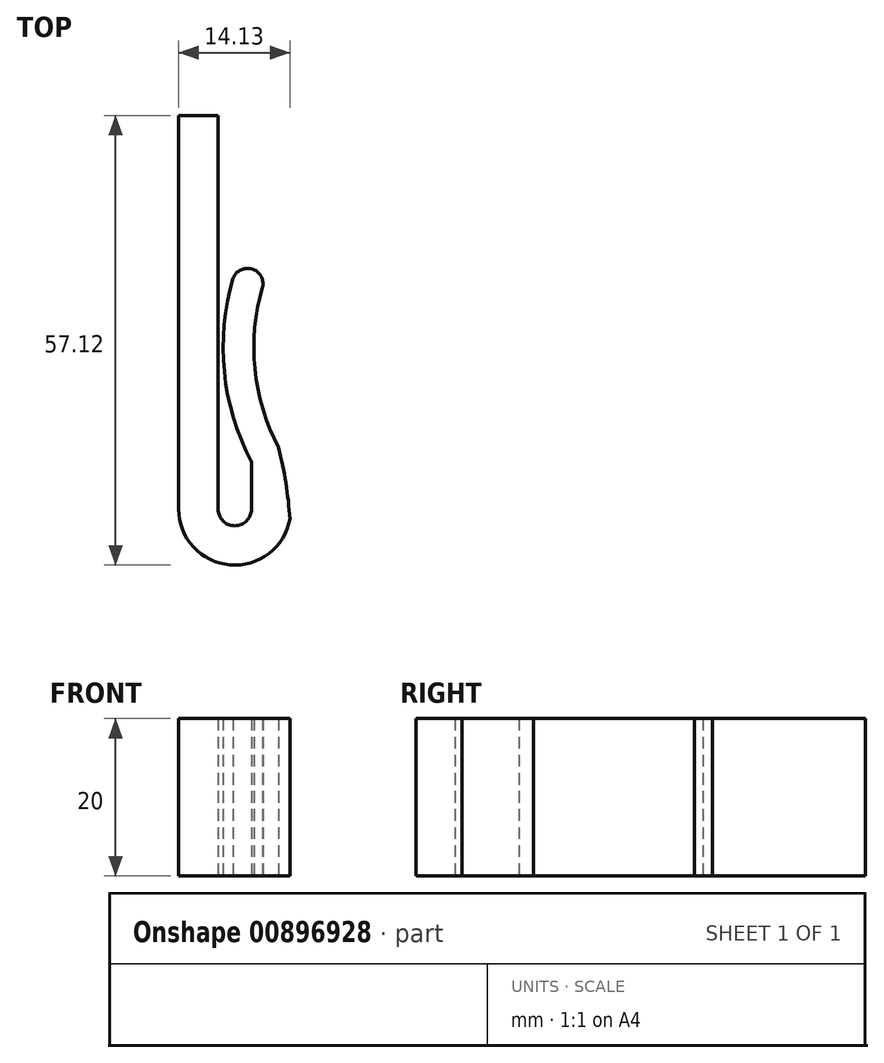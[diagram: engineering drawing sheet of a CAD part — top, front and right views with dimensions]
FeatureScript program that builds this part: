
annotation { "Feature Type Name" : "Feature", "Feature Type Description" : "" }
export const myFeature = defineFeature(function(context is Context, id is Id, definition is map)
    precondition{}
    {
        {
            var Q0;
            Q0=qCreatedBy(makeId("Top.planeOp"),FACE);
            var sketch = newSketch(context, id + "F0", { "sketchPlane" : qUnion([Q0])});
            skLineSegment(sketch, "E0.bottom", {"start": v(-6.12, 38.34) * mm, "end": v(-1.12, 38.34) * mm});
            skLineSegment(sketch, "E0.top", {"start": v(-6.12, -11.66) * mm, "end": v(-1.12, -11.66) * mm});
            skLineSegment(sketch, "E0.left", {"start": v(-6.12, 38.34) * mm, "end": v(-6.12, -11.66) * mm});
            skLineSegment(sketch, "E0.right", {"start": v(-1.12, 38.34) * mm, "end": v(-1.12, -11.66) * mm});
            skArc(sketch, "E1", {"start": v(-6.12, -11.66) * mm, "mid": v(1, -18.78) * mm, "end": v(8.12, -11.66) * mm});
            skArc(sketch, "E2.0", {"start": v(-1.12, -11.66) * mm, "mid": v(1, -13.78) * mm, "end": v(3.12, -11.66) * mm});
            skLineSegment(sketch, "E3", {"start": v(3.12, -11.66) * mm, "end": v(3.12, -5.66) * mm});
            skLineSegment(sketch, "E4", {"start": v(3.12, -5.66) * mm, "end": v(8.12, -5.66) * mm});
            skLineSegment(sketch, "E5", {"start": v(8.12, -5.66) * mm, "end": v(8.12, -11.66) * mm});
            skArc(sketch, "E6", {"start": v(0.8, 17.68) * mm, "mid": v(-0.32, 5.78) * mm, "end": v(3.12, -5.66) * mm});
            skArc(sketch, "E7.0", {"start": v(4.55, 16.58) * mm, "mid": v(3.56, 6.17) * mm, "end": v(6.57, -3.84) * mm});
            skLineSegment(sketch, "E8", {"start": v(6.57, -3.84) * mm, "end": v(8.12, -5.66) * mm});
            skArc(sketch, "E9", {"start": v(4.55, 16.58) * mm, "mid": v(3.18, 18.84) * mm, "end": v(0.8, 17.68) * mm});
            skSolve(sketch);
        }
        {
            var Q0;
            Q0 = qSketchRegion(id + "F0", true);
            extrude(context, id + "F1", {"entities" : qUnion([Q0]), "depth" : 20 * mm, "offsetDistance" : 25 * mm});
        }
        {
            var Q0;
            Q0=makeQuery(id+"F1.opExtrude","SWEPT_EDGE",EDGE,{"disambiguationData":[OSD([sQuery(id+"F0.wireOp",EDGE,"E4"),sQuery(id+"F0.wireOp",EDGE,"E5"),sQuery(id+"F0.wireOp",EDGE,"E8")])]});
            fillet(context, id + "F2", {"entities" : qUnion([Q0]), "radius" : 50.24 * mm, "tangentPropagation" : true, "allowEdgeOverflow" : false});
        }
    });
